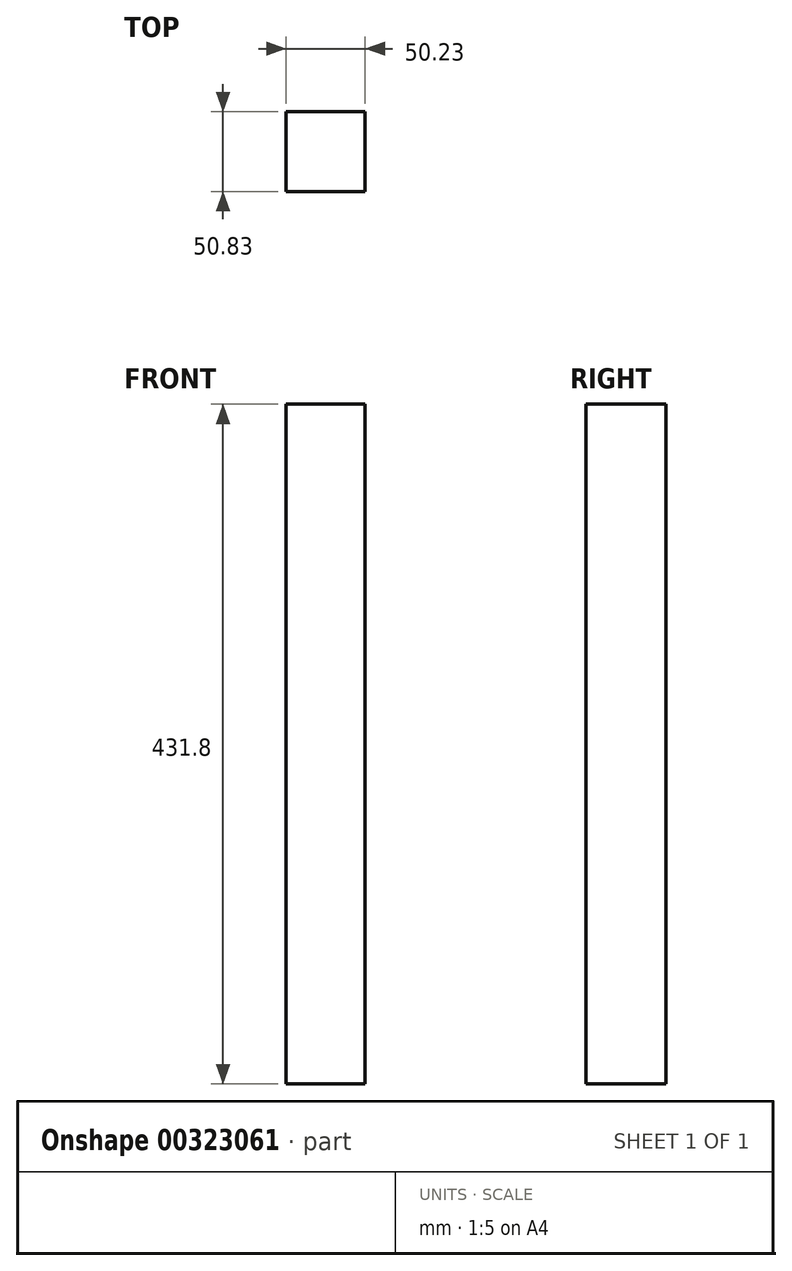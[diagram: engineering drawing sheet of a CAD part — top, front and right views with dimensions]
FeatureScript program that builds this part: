
annotation { "Feature Type Name" : "Feature", "Feature Type Description" : "" }
export const myFeature = defineFeature(function(context is Context, id is Id, definition is map)
    precondition{}
    {
        {
            var Q0;
            Q0=qCreatedBy(makeId("Top.planeOp"),FACE);
            var sketch = newSketch(context, id + "F0", { "sketchPlane" : qUnion([Q0])});
            skLineSegment(sketch, "E0.bottom", {"start": v(-63.77, 50.83) * mm, "end": v(-13.54, 50.83) * mm});
            skLineSegment(sketch, "E0.top", {"start": v(-63.77, 0) * mm, "end": v(-13.54, 0) * mm});
            skLineSegment(sketch, "E0.left", {"start": v(-63.77, 50.83) * mm, "end": v(-63.77, 0) * mm});
            skLineSegment(sketch, "E0.right", {"start": v(-13.54, 50.83) * mm, "end": v(-13.54, 0) * mm});
            skSolve(sketch);
        }
        {
            var Q0;
            Q0=makeQuery(id+"F0.imprint","IMPRINT",FACE,{"disambiguationData":[TD([[makeQuery(id+"F0.imprint","IMPRINT",EDGE,{"derivedFrom":sQuery(id+"F0.wireOp",EDGE,"E0.bottom")}),-1.0]])]});
            extrude(context, id + "F1", {"entities" : qUnion([Q0]), "depth" : 431.8 * mm});
        }
    });
